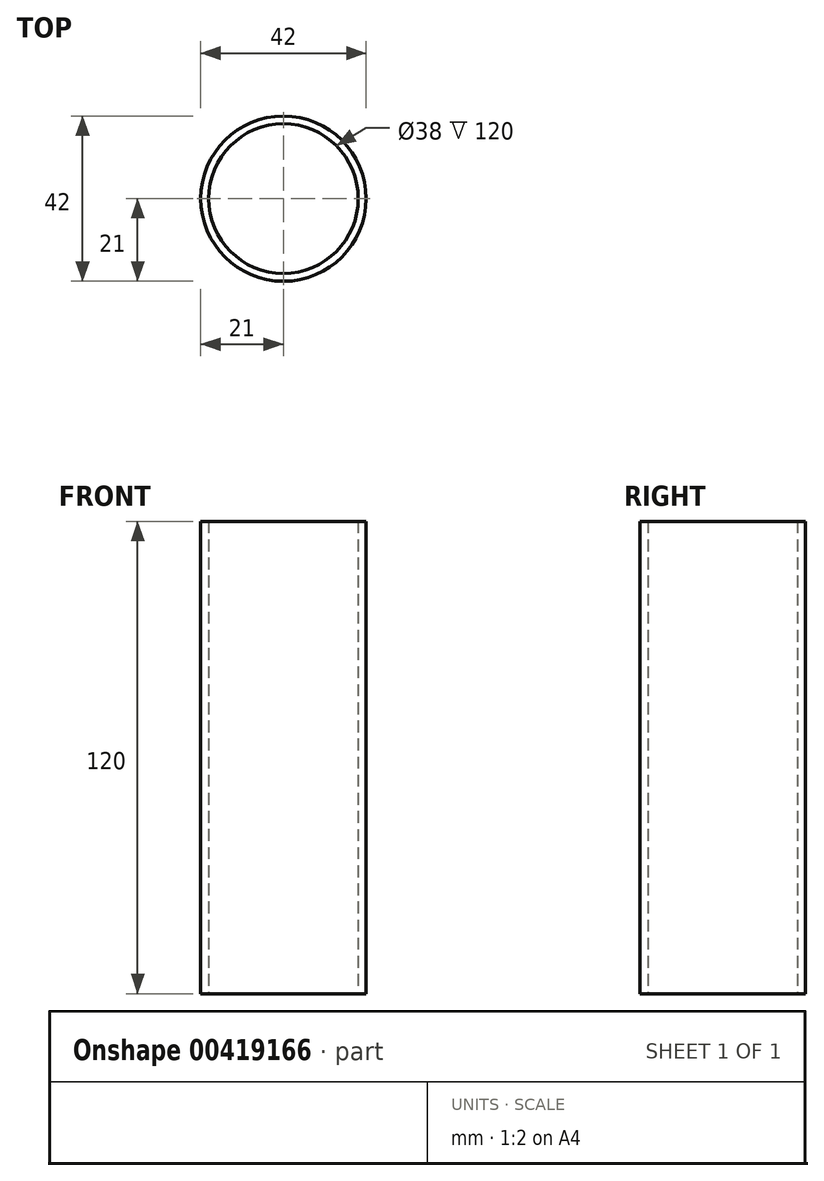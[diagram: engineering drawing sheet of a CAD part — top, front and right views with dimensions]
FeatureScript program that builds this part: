
annotation { "Feature Type Name" : "Feature", "Feature Type Description" : "" }
export const myFeature = defineFeature(function(context is Context, id is Id, definition is map)
    precondition{}
    {
        {
            var Q0;
            Q0=qCreatedBy(makeId("Top.planeOp"),FACE);
            var sketch = newSketch(context, id + "F0", { "sketchPlane" : qUnion([Q0])});
            skCircle(sketch, "E0", {"center": v(0, 0) * mm, "radius": 21 * mm});
            skCircle(sketch, "E1", {"center": v(0, 0) * mm, "radius": 19 * mm});
            skSolve(sketch);
        }
        {
            var Q0;
            Q0 = qSketchRegion(id + "F0", true);
            extrude(context, id + "F1", {"entities" : qUnion([Q0]), "depth" : 120 * mm});
        }
    });
